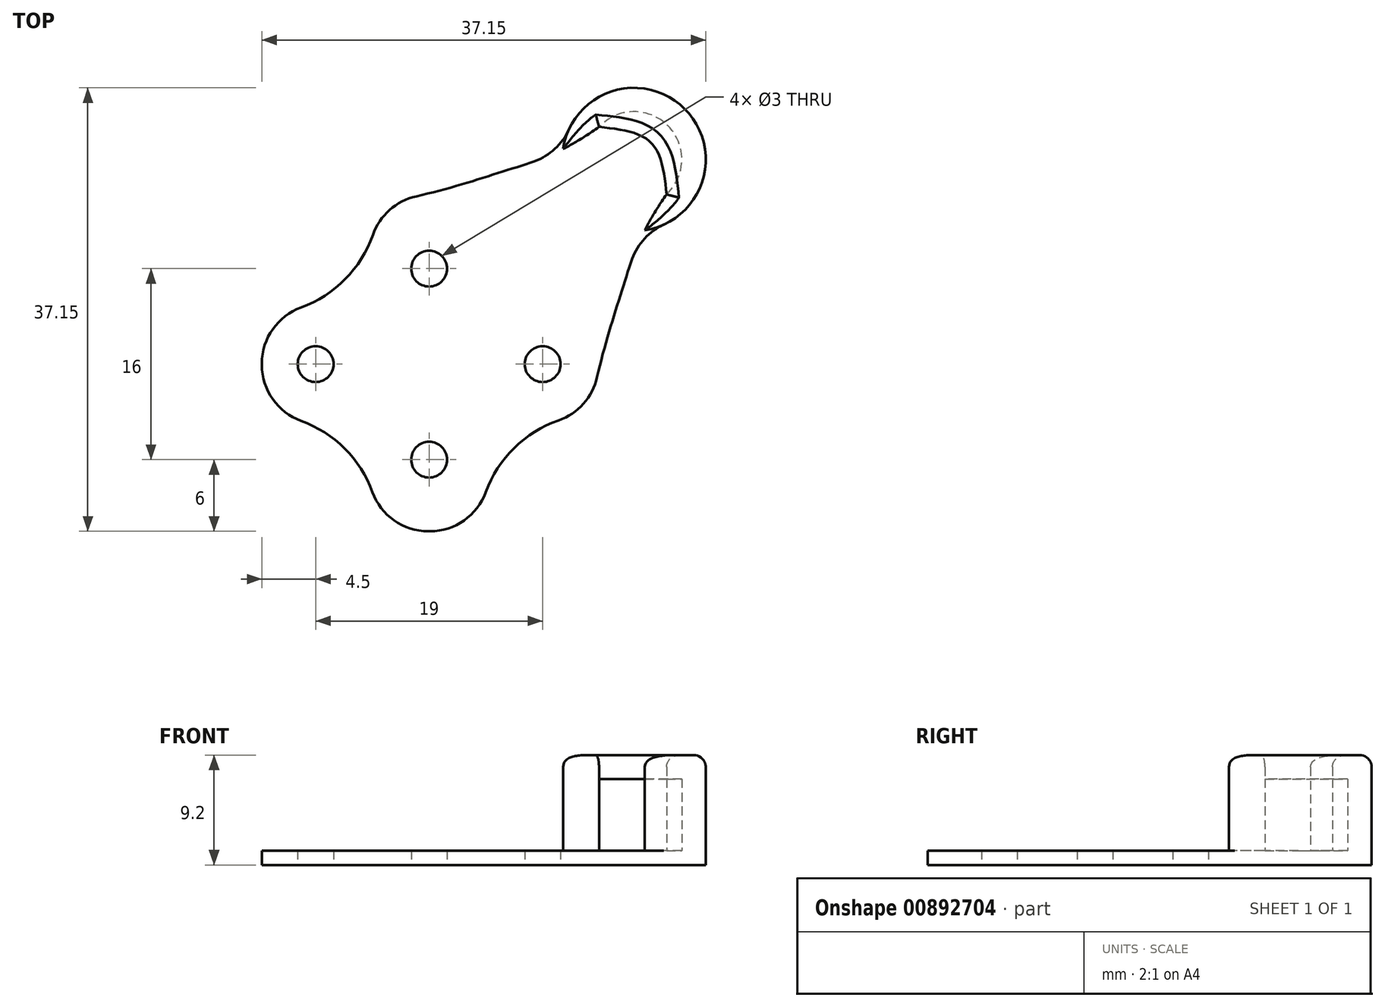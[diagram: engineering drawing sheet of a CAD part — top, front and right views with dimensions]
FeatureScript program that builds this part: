
annotation { "Feature Type Name" : "Feature", "Feature Type Description" : "" }
export const myFeature = defineFeature(function(context is Context, id is Id, definition is map)
    precondition{}
    {
        {
            var Q0;
            Q0=qCreatedBy(makeId("Top.planeOp"),FACE);
            var sketch = newSketch(context, id + "F0", { "sketchPlane" : qUnion([Q0])});
            skArc(sketch, "E0", {"start": v(-13.36, 4.17) * mm, "mid": v(-14, 0) * mm, "end": v(-13.36, -4.17) * mm});
            skCircle(sketch, "E1", {"center": v(17.15, 17.15) * mm, "radius": 4 * mm});
            skCircle(sketch, "E2", {"center": v(17.15, 17.15) * mm, "radius": 6 * mm});
            skCircle(sketch, "E3", {"center": v(9.5, 0) * mm, "radius": 1.5 * mm});
            skCircle(sketch, "E4", {"center": v(0, 8) * mm, "radius": 1.5 * mm});
            skCircle(sketch, "E5", {"center": v(-9.5, 0) * mm, "radius": 1.5 * mm});
            skCircle(sketch, "E6", {"center": v(0, -8) * mm, "radius": 1.5 * mm});
            skFitSpline(sketch, "E7", {"points": [v(14.22, 19.87) * mm, v(6.68, 16.3) * mm, v(-2.02, 13.85) * mm], "startDerivative": vector(-19.43, -13.68) * mm, "endDerivative": vector(-18.68, -3.78) * mm});
            skFitSpline(sketch, "E8.MirrorCS", {"points": [v(19.87, 14.22) * mm, v(16.3, 6.68) * mm, v(13.85, -2.02) * mm], "startDerivative": vector(-13.68, -19.43) * mm, "endDerivative": vector(-3.78, -18.68) * mm});
            skArc(sketch, "E9", {"start": v(-4.17, -13.36) * mm, "mid": v(-7.07, -7.07) * mm, "end": v(-13.36, -4.17) * mm});
            skArc(sketch, "E10", {"start": v(-13.36, 4.17) * mm, "mid": v(-7.07, 7.07) * mm, "end": v(-4.17, 13.36) * mm});
            skArc(sketch, "E11", {"start": v(13.36, -4.17) * mm, "mid": v(7.07, -7.07) * mm, "end": v(4.17, -13.36) * mm});
            skArc(sketch, "E12.trimOffspring", {"start": v(-4.17, -13.36) * mm, "mid": v(0, -14) * mm, "end": v(4.17, -13.36) * mm});
            skArc(sketch, "E13.trimOffspring", {"start": v(13.36, -4.17) * mm, "mid": v(13.65, -3.1) * mm, "end": v(13.85, -2.02) * mm});
            skArc(sketch, "E14.trimOffspring", {"start": v(-2.02, 13.85) * mm, "mid": v(-3.1, 13.65) * mm, "end": v(-4.17, 13.36) * mm});
            skCircle(sketch, "E15", {"center": v(-9.5, 0) * mm, "radius": 3 * mm});
            skCircle(sketch, "E16", {"center": v(0, 8) * mm, "radius": 3 * mm});
            skCircle(sketch, "E17", {"center": v(9.5, 0) * mm, "radius": 3 * mm});
            skCircle(sketch, "E18", {"center": v(0, -8) * mm, "radius": 3 * mm});
            skFitSpline(sketch, "E19", {"points": [v(14.22, 19.87) * mm, v(18.56, 18.56) * mm, v(19.87, 14.22) * mm], "startDerivative": vector(10.2, -1.1) * mm, "endDerivative": vector(1.1, -10.2) * mm});
            skSolve(sketch);
        }
        {
            var Q0;
            Q0=qSketchRegion(id+"F0",true);
            var Q1;
            {var subQ0=sQuery(id+"F0.wireOp",EDGE,"E1");var subQ1=makeQuery(id+"F0.imprint","INTERSECT",VERTEX,{"derivedFrom":[subQ0,sQuery(id+"F0.wireOp",EDGE,"E7")]});Q1=makeQuery(id+"F0.imprint","IMPRINT",FACE,{"disambiguationData":[TD([[makeQuery(id+"F0.imprint","IMPRINT",EDGE,{"disambiguationData":[TD([[subQ1,-1.0]])],"derivedFrom":subQ0}),1.0]])]});}
            var Q2;
            Q2=makeQuery(id+"F0.imprint","IMPRINT",FACE,{"disambiguationData":[TD([[makeQuery(id+"F0.imprint","IMPRINT",EDGE,{"derivedFrom":sQuery(id+"F0.wireOp",EDGE,"E3")}),-1.0]])]});
            var Q3;
            Q3=makeQuery(id+"F0.imprint","IMPRINT",FACE,{"disambiguationData":[TD([[makeQuery(id+"F0.imprint","IMPRINT",EDGE,{"derivedFrom":sQuery(id+"F0.wireOp",EDGE,"E4")}),-1.0]])]});
            var Q4;
            Q4=makeQuery(id+"F0.imprint","IMPRINT",FACE,{"disambiguationData":[TD([[makeQuery(id+"F0.imprint","IMPRINT",EDGE,{"derivedFrom":sQuery(id+"F0.wireOp",EDGE,"E5")}),-1.0]])]});
            var Q5;
            Q5=makeQuery(id+"F0.imprint","IMPRINT",FACE,{"disambiguationData":[TD([[makeQuery(id+"F0.imprint","IMPRINT",EDGE,{"derivedFrom":sQuery(id+"F0.wireOp",EDGE,"E6")}),-1.0]])]});
            var Q6;
            {var subQ0=sQuery(id+"F0.wireOp",EDGE,"8f289a3b-867d-457d-ba58-ada0f91db97e");Q6=makeQuery(id+"F0.imprint","IMPRINT",FACE,{"disambiguationData":[TD([[makeQuery(id+"F0.imprint","IMPRINT",EDGE,{"derivedFrom":subQ0}),1.0]])]});}
            var Q7;
            {var subQ0=sQuery(id+"F0.wireOp",EDGE,"E19");Q7=makeQuery(id+"F0.imprint","IMPRINT",FACE,{"disambiguationData":[TD([[makeQuery(id+"F0.imprint","IMPRINT",EDGE,{"derivedFrom":subQ0}),1.0]])]});}
            extrude(context, id + "F1", {"entities" : qUnion([Q0, Q1, Q2, Q3, Q4, Q5, Q6, Q7]), "depth" : 1.2 * mm, "offsetDistance" : 25 * mm});
        }
        {
            var Q0;
            Q0=makeQuery(id+"F1.opExtrude","SWEPT_EDGE",EDGE,{"disambiguationData":[OSD([sQuery(id+"F0.wireOp",EDGE,"E2"),sQuery(id+"F0.wireOp",EDGE,"E7")])]});
            var Q1;
            Q1=makeQuery(id+"F1.opExtrude","SWEPT_EDGE",EDGE,{"disambiguationData":[OSD([sQuery(id+"F0.wireOp",EDGE,"E2"),sQuery(id+"F0.wireOp",EDGE,"E8.MirrorCS")])]});
            var Q2;
            Q2=makeQuery(id+"F1.opExtrude","SWEPT_EDGE",EDGE,{"disambiguationData":[OSD([sQuery(id+"F0.wireOp",EDGE,"E10"),sQuery(id+"F0.wireOp",EDGE,"E14.trimOffspring")])]});
            var Q3;
            Q3=makeQuery(id+"F1.opExtrude","SWEPT_EDGE",EDGE,{"disambiguationData":[OSD([sQuery(id+"F0.wireOp",EDGE,"E0"),sQuery(id+"F0.wireOp",EDGE,"E10")])]});
            var Q4;
            Q4=makeQuery(id+"F1.opExtrude","SWEPT_EDGE",EDGE,{"disambiguationData":[OSD([sQuery(id+"F0.wireOp",EDGE,"E0"),sQuery(id+"F0.wireOp",EDGE,"E9")])]});
            var Q5;
            Q5=makeQuery(id+"F1.opExtrude","SWEPT_EDGE",EDGE,{"disambiguationData":[OSD([sQuery(id+"F0.wireOp",EDGE,"E9"),sQuery(id+"F0.wireOp",EDGE,"E12.trimOffspring")])]});
            var Q6;
            Q6=makeQuery(id+"F1.opExtrude","SWEPT_EDGE",EDGE,{"disambiguationData":[OSD([sQuery(id+"F0.wireOp",EDGE,"E11"),sQuery(id+"F0.wireOp",EDGE,"E12.trimOffspring")])]});
            var Q7;
            Q7=makeQuery(id+"F1.opExtrude","SWEPT_EDGE",EDGE,{"disambiguationData":[OSD([sQuery(id+"F0.wireOp",EDGE,"E11"),sQuery(id+"F0.wireOp",EDGE,"E13.trimOffspring")])]});
            fillet(context, id + "F2", {"entities" : qUnion([Q0, Q1, Q2, Q3, Q4, Q5, Q6, Q7]), "radius" : 5 * mm, "tangentPropagation" : true, "allowEdgeOverflow" : false});
        }
        {
            var Q0;
            {var subQ1=sQuery(id+"F0.wireOp",EDGE,"E7");var subQ6=sQuery(id+"F0.wireOp",EDGE,"E2");var subQ7=makeQuery(id+"F0.imprint","INTERSECT",VERTEX,{"derivedFrom":[subQ6,subQ1]});Q0=makeQuery(id+"F0.imprint","IMPRINT",FACE,{"disambiguationData":[TD([[makeQuery(id+"F0.imprint","IMPRINT",EDGE,{"disambiguationData":[TD([[subQ7,1.0]])],"derivedFrom":subQ6}),1.0]])]});}
            var Q1;
            {var subQ0=sQuery(id+"F0.wireOp",EDGE,"E19");Q1=makeQuery(id+"F0.imprint","IMPRINT",FACE,{"disambiguationData":[TD([[makeQuery(id+"F0.imprint","IMPRINT",EDGE,{"derivedFrom":subQ0}),1.0]])]});}
            extrude(context, id + "F3", {"entities" : qUnion([Q0, Q1]), "operationType" : NewBodyOperationType.ADD, "depth" : 9.2 * mm, "offsetDistance" : 25 * mm});
        }
        {
            var Q0;
            {var subQ0=sQuery(id+"F0.wireOp",EDGE,"E19");Q0=makeQuery(id+"F0.imprint","IMPRINT",FACE,{"disambiguationData":[TD([[makeQuery(id+"F0.imprint","IMPRINT",EDGE,{"derivedFrom":subQ0}),1.0]])]});}
            extrude(context, id + "F4", {"entities" : qUnion([Q0]), "operationType" : NewBodyOperationType.REMOVE, "oppositeDirection" : true, "depth" : -7.2 * mm, "offsetDistance" : 25 * mm, "hasSecondDirection" : true, "secondDirectionOppositeDirection" : false, "secondDirectionDepth" : 1.2 * mm});
        }
        {
            var Q0;
            Q0=makeQuery(id+"F3.opExtrude","CAP_EDGE",EDGE,{"disambiguationData":[OSD([sQuery(id+"F0.wireOp",EDGE,"E2")])],"isStart":false});
            var Q1;
            Q1=makeQuery(id+"F3.opExtrude","CAP_EDGE",EDGE,{"disambiguationData":[OSD([sQuery(id+"F0.wireOp",EDGE,"E19")])],"isStart":false});
            var Q2;
            Q2=makeQuery(id+"F3.opExtrude","CAP_EDGE",EDGE,{"disambiguationData":[OSD([sQuery(id+"F0.wireOp",EDGE,"E8.MirrorCS")])],"isStart":false});
            var Q3;
            Q3=makeQuery(id+"F3.opExtrude","CAP_EDGE",EDGE,{"disambiguationData":[OSD([sQuery(id+"F0.wireOp",EDGE,"E7")])],"isStart":false});
            fillet(context, id + "F5", {"entities" : qUnion([Q0, Q1, Q2, Q3]), "radius" : 1 * mm, "tangentPropagation" : true, "allowEdgeOverflow" : false});
        }
    });
